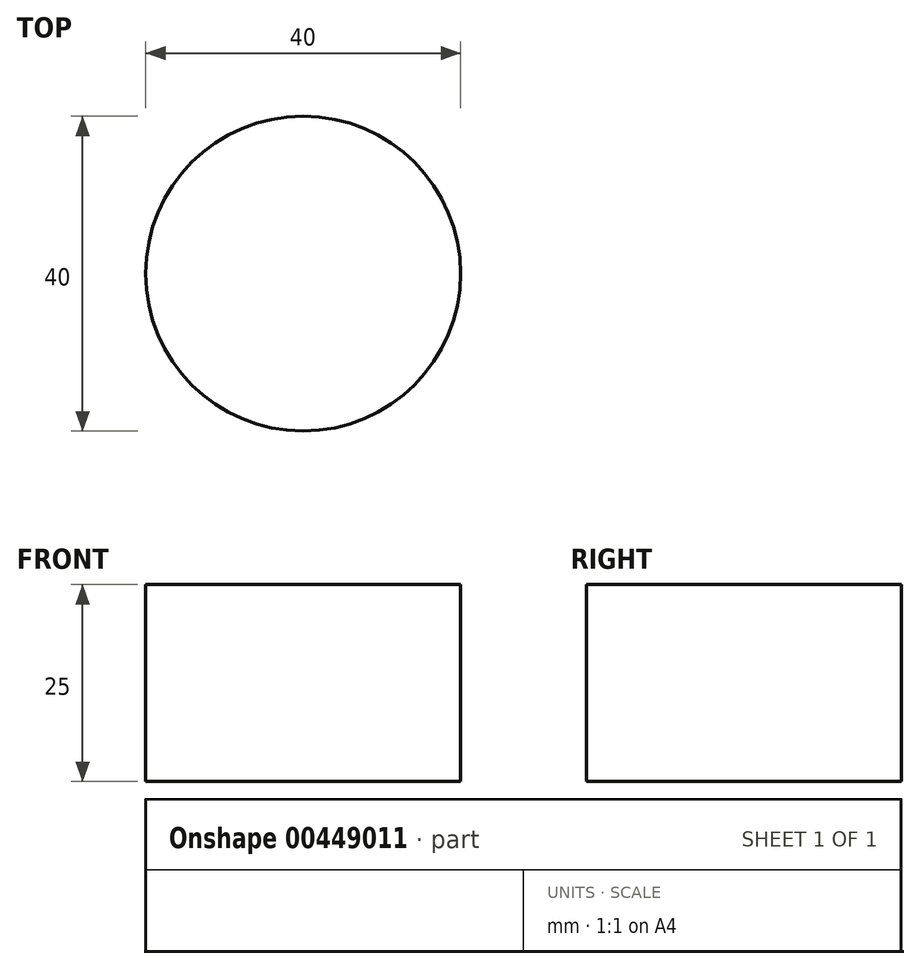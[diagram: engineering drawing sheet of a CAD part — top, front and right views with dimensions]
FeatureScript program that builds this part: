
annotation { "Feature Type Name" : "Feature", "Feature Type Description" : "" }
export const myFeature = defineFeature(function(context is Context, id is Id, definition is map)
    precondition{}
    {
        {
            var Q0;
            Q0=qCreatedBy(makeId("Top.planeOp"),FACE);
            var sketch = newSketch(context, id + "F0", { "sketchPlane" : qUnion([Q0])});
            skLineSegment(sketch, "E0.bottom", {"start": v(-39.8, 39.8) * mm, "end": v(39.8, 39.8) * mm});
            skLineSegment(sketch, "E0.top", {"start": v(-39.8, -39.8) * mm, "end": v(39.8, -39.8) * mm});
            skLineSegment(sketch, "E0.left", {"start": v(-39.8, 39.8) * mm, "end": v(-39.8, -39.8) * mm});
            skLineSegment(sketch, "E0.right", {"start": v(39.8, 39.8) * mm, "end": v(39.8, -39.8) * mm});
            skPoint(sketch, "E0.middle", {"position": v(0, 0) * mm});
            skLineSegment(sketch, "E1.bottom", {"start": v(77.43, 39.8) * mm, "end": v(153.77, 39.8) * mm});
            skLineSegment(sketch, "E1.top", {"start": v(77.43, -39.8) * mm, "end": v(153.77, -39.8) * mm});
            skLineSegment(sketch, "E1.left", {"start": v(77.43, 39.8) * mm, "end": v(77.43, -39.8) * mm});
            skLineSegment(sketch, "E1.right", {"start": v(153.77, 39.8) * mm, "end": v(153.77, -39.8) * mm});
            skPoint(sketch, "E1.middle", {"position": v(115.6, 0) * mm});
            skLineSegment(sketch, "E2.bottom", {"start": v(197, 39.8) * mm, "end": v(270.75, 39.8) * mm});
            skLineSegment(sketch, "E2.top", {"start": v(197, -39.8) * mm, "end": v(270.75, -39.8) * mm});
            skLineSegment(sketch, "E2.left", {"start": v(197, 39.8) * mm, "end": v(197, -39.8) * mm});
            skLineSegment(sketch, "E2.right", {"start": v(270.75, 39.8) * mm, "end": v(270.75, -39.8) * mm});
            skPoint(sketch, "E2.middle", {"position": v(233.87, 0) * mm});
            skLineSegment(sketch, "E3.bottom", {"start": v(310.29, 39.8) * mm, "end": v(393.65, 39.8) * mm});
            skLineSegment(sketch, "E3.top", {"start": v(310.29, -39.8) * mm, "end": v(393.65, -39.8) * mm});
            skLineSegment(sketch, "E3.left", {"start": v(310.29, 39.8) * mm, "end": v(310.29, -39.8) * mm});
            skLineSegment(sketch, "E3.right", {"start": v(393.65, 39.8) * mm, "end": v(393.65, -39.8) * mm});
            skPoint(sketch, "E3.middle", {"position": v(351.97, 0) * mm});
            skSolve(sketch);
        }
        {
            var Q0;
            Q0 = qSketchRegion(id + "F0", true);
            extrude(context, id + "F1", {"entities" : qUnion([Q0]), "depth" : 25 * mm});
        }
        {
            var Q0;
            Q0=qCreatedBy(makeId("Top.planeOp"),FACE);
            var sketch = newSketch(context, id + "F2", { "sketchPlane" : qUnion([Q0])});
            skCircle(sketch, "E4", {"center": v(233.87, 0) * mm, "radius": 20 * mm});
            skPoint(sketch, "E4.centerSnap0", {"position": v(233.87, 39.8) * mm});
            skPoint(sketch, "E4.centerSnap1", {"position": v(270.75, 0) * mm});
            skPoint(sketch, "E5.0", {"position": v(0, 39.8) * mm});
            skPoint(sketch, "E6.0", {"position": v(115.6, 39.8) * mm});
            skCircle(sketch, "E7", {"center": v(0, 0) * mm, "radius": 20 * mm});
            skCircle(sketch, "E8", {"center": v(115.6, 0) * mm, "radius": 20 * mm});
            skLineSegment(sketch, "E9.0", {"start": v(310.29, 39.8) * mm, "end": v(393.65, 39.8) * mm});
            skLineSegment(sketch, "E10.0.0", {"start": v(310.29, 39.8) * mm, "end": v(310.29, -39.8) * mm});
            skLineSegment(sketch, "E10.0.1", {"start": v(310.29, -39.8) * mm, "end": v(393.65, -39.8) * mm});
            skLineSegment(sketch, "E10.0.2", {"start": v(393.65, -39.8) * mm, "end": v(393.65, 39.8) * mm});
            skLineSegment(sketch, "E10.0.3", {"start": v(393.65, 39.8) * mm, "end": v(310.29, 39.8) * mm});
            skPoint(sketch, "E11", {"position": v(351.97, 39.8) * mm});
            skCircle(sketch, "E12", {"center": v(351.97, 0) * mm, "radius": 20 * mm});
            skSolve(sketch);
        }
        {
            var Q0;
            Q0=makeQuery(id+"F2.imprint","IMPRINT",FACE,{"disambiguationData":[TD([[makeQuery(id+"F2.imprint","IMPRINT",EDGE,{"derivedFrom":sQuery(id+"F2.wireOp",EDGE,"E7")}),1.0]])]});
            extrude(context, id + "F3", {"entities" : qUnion([Q0]), "depth" : 50 * mm});
        }
        {
            var Q0;
            Q0=makeQuery(id+"F2.imprint","IMPRINT",FACE,{"disambiguationData":[TD([[makeQuery(id+"F2.imprint","IMPRINT",EDGE,{"derivedFrom":sQuery(id+"F2.wireOp",EDGE,"E8")}),1.0]])]});
            extrude(context, id + "F4", {"entities" : qUnion([Q0]), "operationType" : NewBodyOperationType.ADD, "depth" : 50 * mm});
        }
        {
            var Q0;
            Q0=makeQuery(id+"F2.imprint","IMPRINT",FACE,{"disambiguationData":[TD([[makeQuery(id+"F2.imprint","IMPRINT",EDGE,{"derivedFrom":sQuery(id+"F2.wireOp",EDGE,"E4")}),1.0]])]});
            extrude(context, id + "F5", {"entities" : qUnion([Q0]), "operationType" : NewBodyOperationType.REMOVE, "depth" : 50 * mm});
        }
        {
            var Q0;
            Q0=makeQuery(id+"F2.imprint","IMPRINT",FACE,{"disambiguationData":[TD([[makeQuery(id+"F2.imprint","IMPRINT",EDGE,{"derivedFrom":sQuery(id+"F2.wireOp",EDGE,"E12")}),1.0]])]});
            extrude(context, id + "F6", {"entities" : qUnion([Q0]), "operationType" : NewBodyOperationType.INTERSECT, "depth" : 50 * mm});
        }
    });
